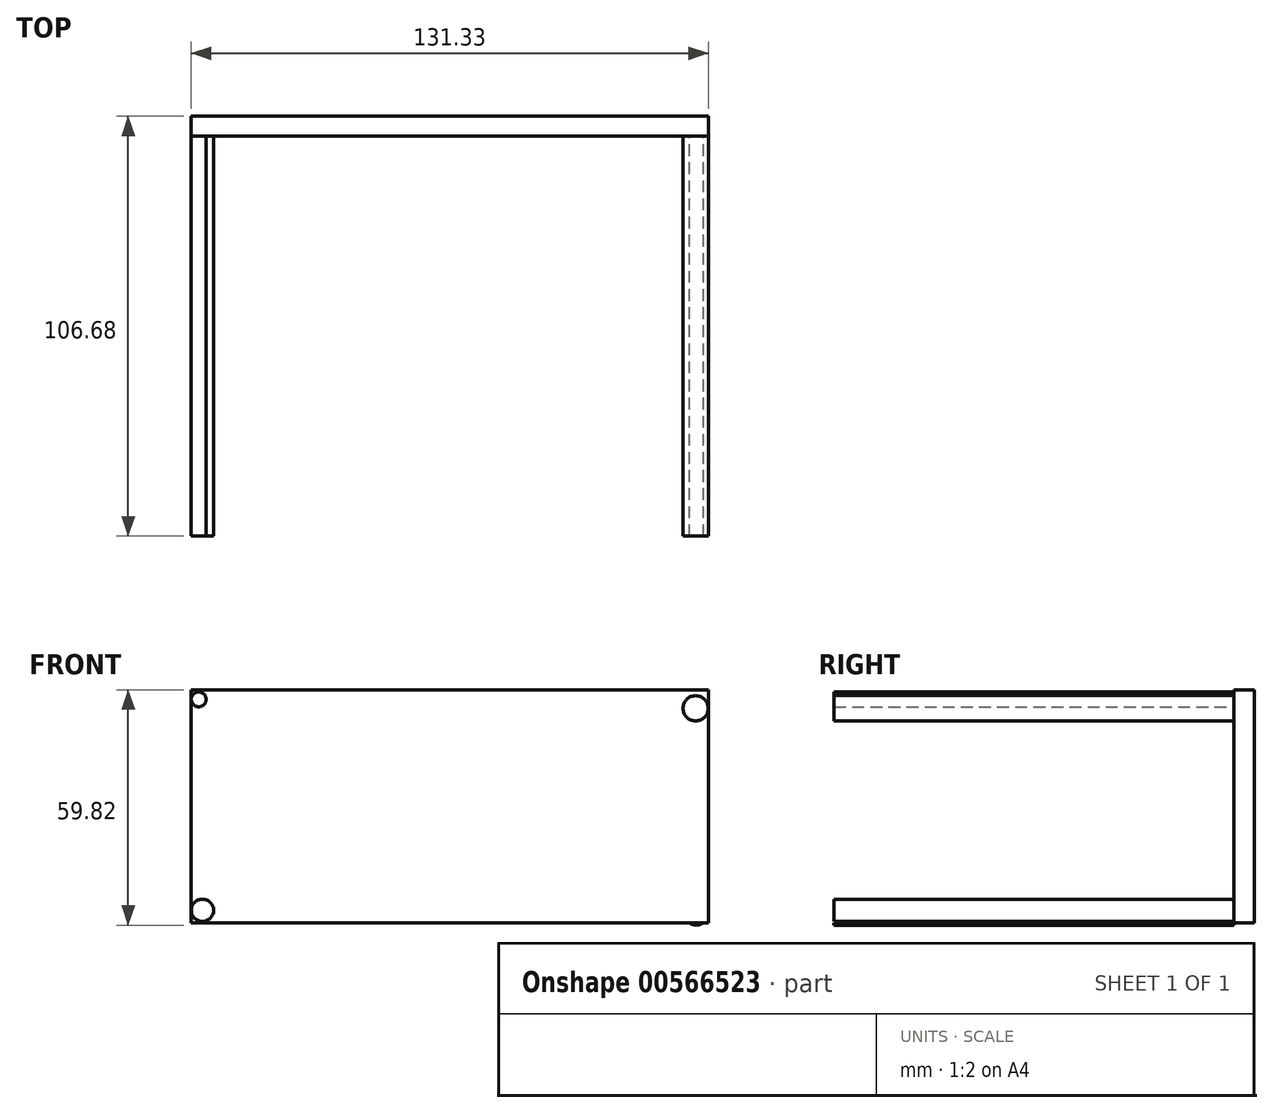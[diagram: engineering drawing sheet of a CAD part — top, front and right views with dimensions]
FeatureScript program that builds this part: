
annotation { "Feature Type Name" : "Feature", "Feature Type Description" : "" }
export const myFeature = defineFeature(function(context is Context, id is Id, definition is map)
    precondition{}
    {
        {
            var Q0;
            Q0=qCreatedBy(makeId("Front.planeOp"),FACE);
            var sketch = newSketch(context, id + "F0", { "sketchPlane" : qUnion([Q0])});
            skLineSegment(sketch, "E0.bottom", {"start": v(-60.57, 54.54) * mm, "end": v(70.76, 54.54) * mm});
            skLineSegment(sketch, "E0.top", {"start": v(-60.57, -4.72) * mm, "end": v(70.76, -4.72) * mm});
            skLineSegment(sketch, "E0.left", {"start": v(-60.57, 54.54) * mm, "end": v(-60.57, -4.72) * mm});
            skLineSegment(sketch, "E0.right", {"start": v(70.76, 54.54) * mm, "end": v(70.76, -4.72) * mm});
            skSolve(sketch);
        }
        {
            var Q0;
            Q0=makeQuery(id+"F0.imprint","IMPRINT",FACE,{"disambiguationData":[TD([[makeQuery(id+"F0.imprint","IMPRINT",EDGE,{"derivedFrom":sQuery(id+"F0.wireOp",EDGE,"E0.bottom")}),-1.0]])]});
            extrude(context, id + "F1", {"entities" : qUnion([Q0]), "depth" : 5.08 * mm, "offsetDistance" : 25.4 * mm});
        }
        {
            var Q0;
            Q0=makeQuery(id+"F1.opExtrude","CAP_FACE",FACE,{"disambiguationData":[OSD([sQuery(id+"F0.wireOp",EDGE,"E0.bottom"),sQuery(id+"F0.wireOp",EDGE,"E0.top"),sQuery(id+"F0.wireOp",EDGE,"E0.left"),sQuery(id+"F0.wireOp",EDGE,"E0.right")])],"isStart":false});
            var sketch = newSketch(context, id + "F2", { "sketchPlane" : qUnion([Q0])});
            skCircle(sketch, "E1", {"center": v(-58.69, 52.08) * mm, "radius": 1.89 * mm});
            skLineSegment(sketch, "E2", {"start": v(0, 54.54) * mm, "end": v(0, -4.72) * mm});
            skCircle(sketch, "E3", {"center": v(67.56, 49.82) * mm, "radius": 3.2 * mm});
            skCircle(sketch, "E4", {"center": v(-57.74, -1.5) * mm, "radius": 2.83 * mm});
            skCircle(sketch, "E5", {"center": v(67.74, -2.26) * mm, "radius": 3.02 * mm});
            skSolve(sketch);
        }
        {
            var Q0;
            Q0=makeQuery(id+"F2.imprint","IMPRINT",FACE,{"disambiguationData":[TD([[makeQuery(id+"F2.imprint","IMPRINT",EDGE,{"derivedFrom":sQuery(id+"F2.wireOp",EDGE,"E1")}),1.0]])]});
            var Q1;
            Q1=makeQuery(id+"F2.imprint","IMPRINT",FACE,{"disambiguationData":[TD([[makeQuery(id+"F2.imprint","IMPRINT",EDGE,{"derivedFrom":sQuery(id+"F2.wireOp",EDGE,"E4")}),1.0]])]});
            var Q2;
            Q2=makeQuery(id+"F2.imprint","IMPRINT",FACE,{"disambiguationData":[TD([[makeQuery(id+"F2.imprint","IMPRINT",EDGE,{"derivedFrom":sQuery(id+"F2.wireOp",EDGE,"E3")}),1.0]])]});
            var Q3;
            {var subQ0=sQuery(id+"F2.wireOp",EDGE,"E5");var subQ1=makeQuery(id+"F1.opExtrude","CAP_EDGE",EDGE,{"disambiguationData":[OSD([sQuery(id+"F0.wireOp",EDGE,"E0.top")])],"isStart":false});var subQ2=makeQuery(id+"F2.imprint","INTERSECT",VERTEX,{"disambiguationData":[OD(0.0)],"derivedFrom":[subQ1,subQ0]});Q3=makeQuery(id+"F2.imprint","IMPRINT",FACE,{"disambiguationData":[TD([[makeQuery(id+"F2.imprint","IMPRINT",EDGE,{"disambiguationData":[TD([[subQ2,1.0]])],"derivedFrom":subQ0}),1.0]])]});}
            extrude(context, id + "F3", {"entities" : qUnion([Q0, Q1, Q2, Q3]), "operationType" : NewBodyOperationType.ADD, "depth" : 101.6 * mm, "offsetDistance" : 25.4 * mm});
        }
    });
